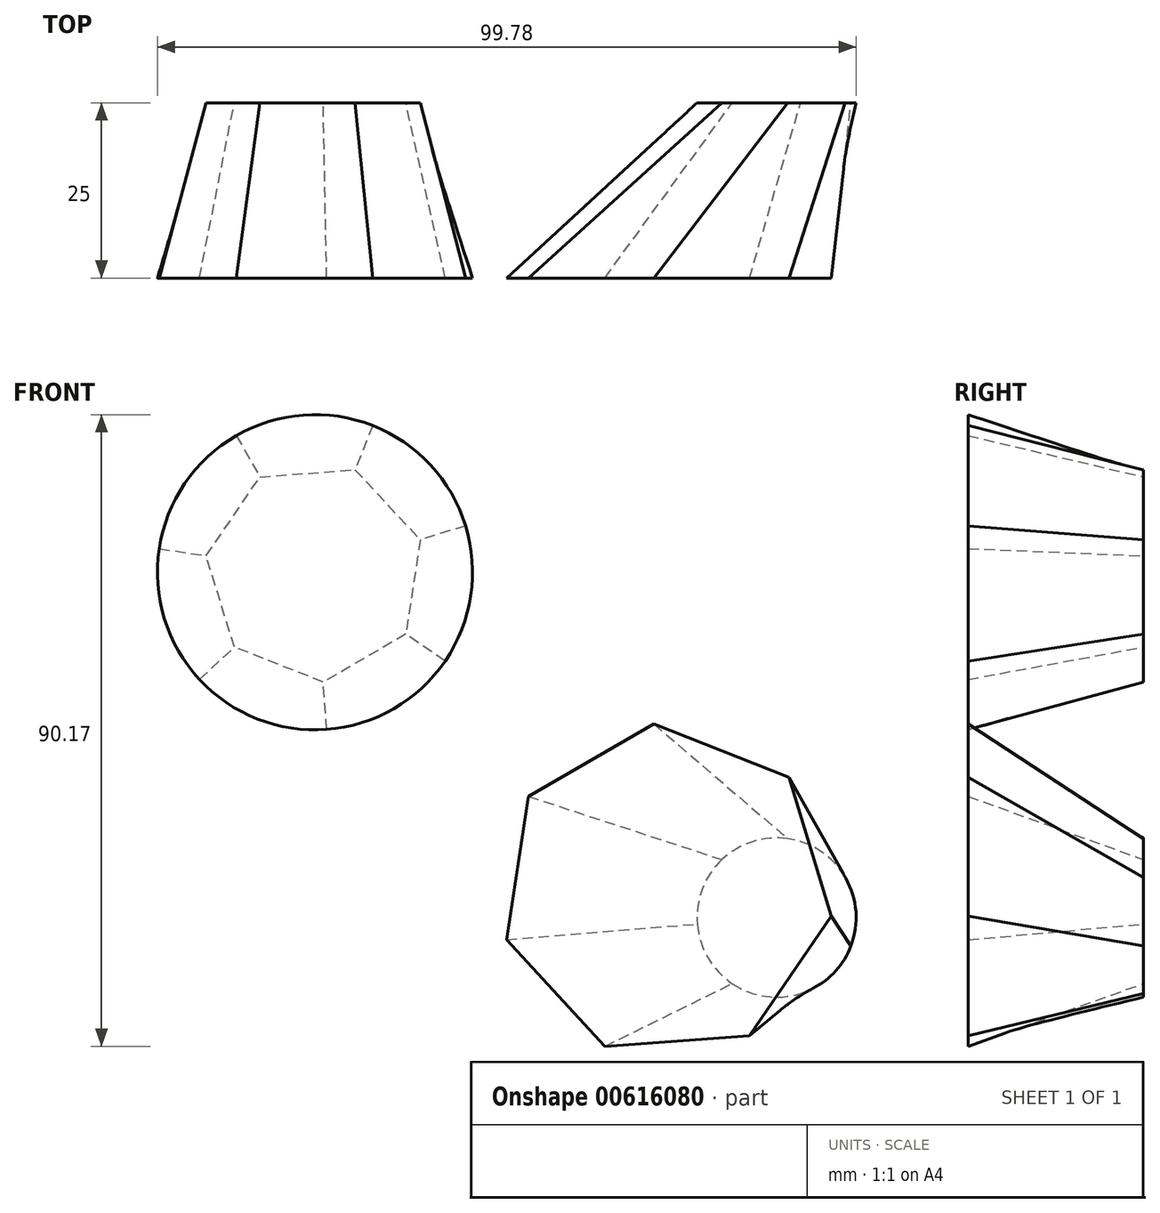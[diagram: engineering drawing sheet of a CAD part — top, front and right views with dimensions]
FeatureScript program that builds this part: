
annotation { "Feature Type Name" : "Feature", "Feature Type Description" : "" }
export const myFeature = defineFeature(function(context is Context, id is Id, definition is map)
    precondition{}
    {
        {
            var Q0;
            Q0=qCreatedBy(makeId("Front.planeOp"),FACE);
            var sketch = newSketch(context, id + "F0", { "sketchPlane" : qUnion([Q0])});
            skCircle(sketch, "E0.cCircle", {"center": v(0, 0) * mm, "radius": 14.16 * mm, "construction": true});
            skLineSegment(sketch, "E0.0", {"start": v(12.98, -8.85) * mm, "end": v(1.17, -15.67) * mm});
            skLineSegment(sketch, "E0.1", {"start": v(1.17, -15.67) * mm, "end": v(-11.52, -10.68) * mm});
            skLineSegment(sketch, "E0.2", {"start": v(-11.52, -10.68) * mm, "end": v(-15.53, 2.35) * mm});
            skLineSegment(sketch, "E0.3", {"start": v(-15.53, 2.35) * mm, "end": v(-7.85, 13.6) * mm});
            skLineSegment(sketch, "E0.4", {"start": v(-7.85, 13.6) * mm, "end": v(5.74, 14.62) * mm});
            skLineSegment(sketch, "E0.5", {"start": v(5.74, 14.62) * mm, "end": v(15.01, 4.63) * mm});
            skLineSegment(sketch, "E0.6", {"start": v(15.01, 4.63) * mm, "end": v(12.98, -8.85) * mm});
            skPoint(sketch, "E0.0.midPoint", {"position": v(7.07, -12.26) * mm});
            skSolve(sketch);
        }
        {
            var Q0;
            Q0=qCreatedBy(makeId("Front.planeOp"),FACE);
            cPlane(context, id + "F1", {"entities" : qUnion([Q0]), "cplaneType" : CPlaneType.OFFSET, "offset" : 25 * mm, "width" : 152.4 * mm, "height" : 152.4 * mm});
        }
        {
            var Q0;
            Q0=qCreatedBy(id+"F1.planeOp",FACE);
            var sketch = newSketch(context, id + "F2", { "sketchPlane" : qUnion([Q0])});
            skCircle(sketch, "E1", {"center": v(0, 0) * mm, "radius": 22.5 * mm});
            skSolve(sketch);
        }
        {
            var Q0;
            Q0=makeQuery(id+"F2.imprint","IMPRINT",FACE,{"disambiguationData":[TD([[makeQuery(id+"F2.imprint","IMPRINT",EDGE,{"derivedFrom":sQuery(id+"F2.wireOp",EDGE,"E1")}),1.0]])]});
            var Q1;
            Q1=makeQuery(id+"F0.imprint","IMPRINT",FACE,{"disambiguationData":[TD([[makeQuery(id+"F0.imprint","IMPRINT",EDGE,{"derivedFrom":sQuery(id+"F0.wireOp",EDGE,"E0.0")}),-1.0]])]});
            loft(context, id + "F3", {"sheetProfilesArray" : [{ "sheetProfileEntities" : qUnion([Q0]) }, { "sheetProfileEntities" : qUnion([Q1]) }]});
        }
        {
            var Q0;
            Q0=qCreatedBy(id+"F1.planeOp",FACE);
            var sketch = newSketch(context, id + "F4", { "sketchPlane" : qUnion([Q0])});
            skCircle(sketch, "E2.cCircle", {"center": v(50.15, -45.47) * mm, "radius": 23.86 * mm, "construction": true});
            skLineSegment(sketch, "E2.0", {"start": v(27.33, -52.46) * mm, "end": v(30.46, -32) * mm});
            skLineSegment(sketch, "E2.1", {"start": v(30.46, -32) * mm, "end": v(48.4, -21.67) * mm});
            skLineSegment(sketch, "E2.2", {"start": v(48.4, -21.67) * mm, "end": v(67.67, -29.27) * mm});
            skLineSegment(sketch, "E2.3", {"start": v(67.67, -29.27) * mm, "end": v(73.74, -49.07) * mm});
            skLineSegment(sketch, "E2.4", {"start": v(73.74, -49.07) * mm, "end": v(62.04, -66.16) * mm});
            skLineSegment(sketch, "E2.5", {"start": v(62.04, -66.16) * mm, "end": v(41.39, -67.67) * mm});
            skLineSegment(sketch, "E2.6", {"start": v(41.39, -67.67) * mm, "end": v(27.33, -52.46) * mm});
            skSolve(sketch);
        }
        {
            var Q0;
            Q0=qCreatedBy(makeId("Front.planeOp"),FACE);
            var sketch = newSketch(context, id + "F5", { "sketchPlane" : qUnion([Q0])});
            skCircle(sketch, "E3", {"center": v(65.91, -49.3) * mm, "radius": 11.36 * mm});
            skSolve(sketch);
        }
        {
            var Q0;
            Q0=makeQuery(id+"F4.imprint","IMPRINT",FACE,{"disambiguationData":[TD([[makeQuery(id+"F4.imprint","IMPRINT",EDGE,{"derivedFrom":sQuery(id+"F4.wireOp",EDGE,"E2.0")}),-1.0]])]});
            var Q1;
            Q1=makeQuery(id+"F5.imprint","IMPRINT",FACE,{"disambiguationData":[TD([[makeQuery(id+"F5.imprint","IMPRINT",EDGE,{"derivedFrom":sQuery(id+"F5.wireOp",EDGE,"E3")}),1.0]])]});
            loft(context, id + "F6", {"sheetProfilesArray" : [{ "sheetProfileEntities" : qUnion([Q0]) }, { "sheetProfileEntities" : qUnion([Q1]) }]});
        }
    });
